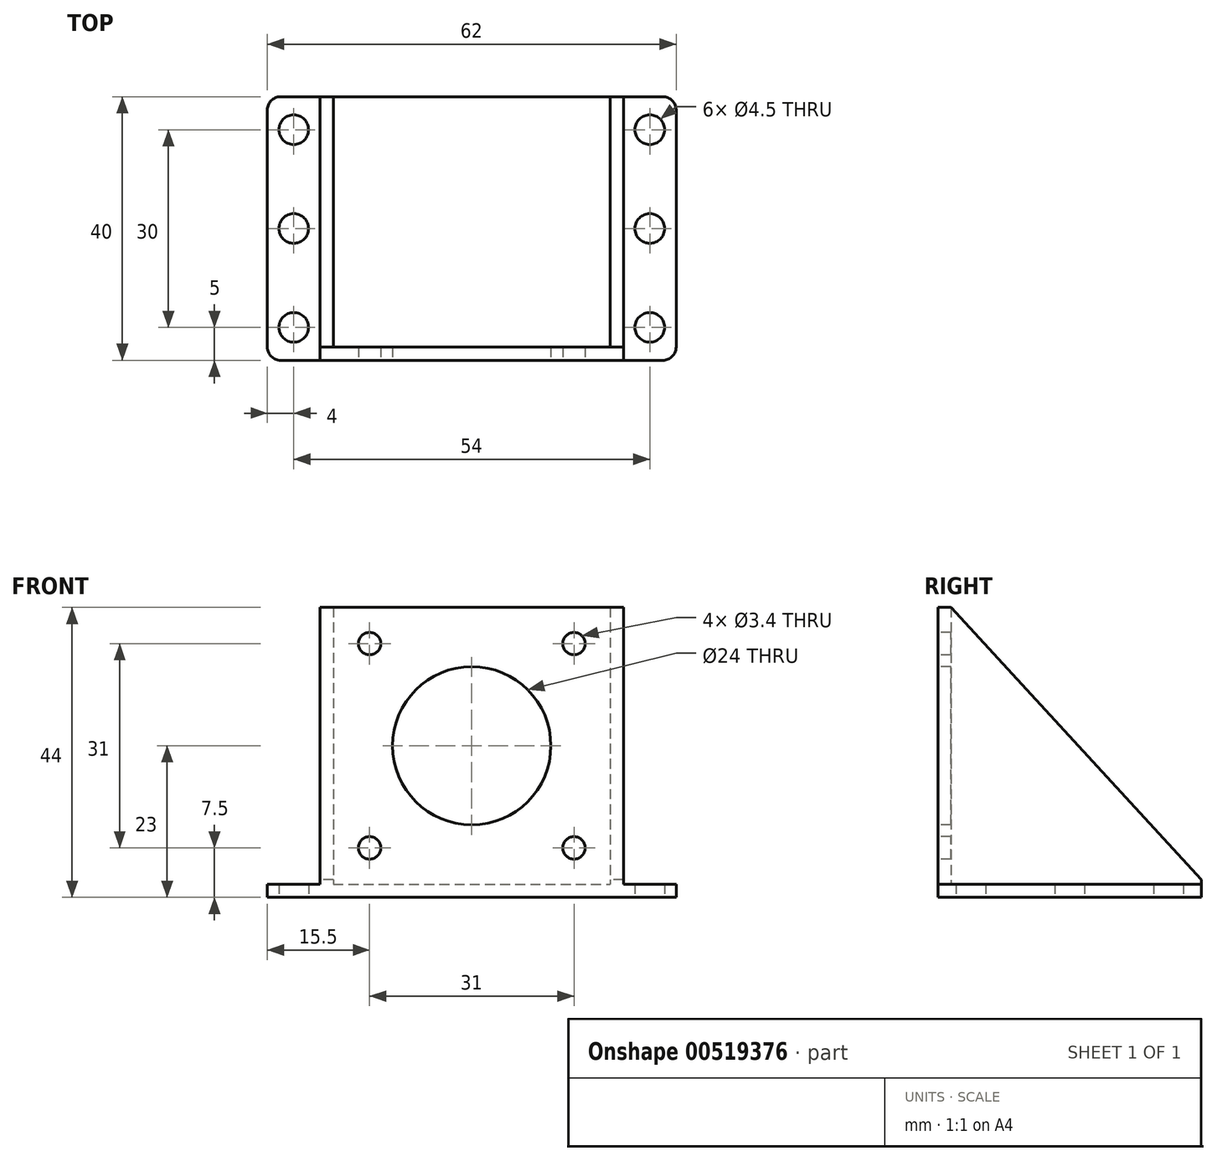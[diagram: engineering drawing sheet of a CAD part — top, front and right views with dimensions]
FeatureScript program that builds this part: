
annotation { "Feature Type Name" : "Feature", "Feature Type Description" : "" }
export const myFeature = defineFeature(function(context is Context, id is Id, definition is map)
    precondition{}
    {
        {
            var Q0;
            Q0=qCreatedBy(makeId("Top.planeOp"),FACE);
            var sketch = newSketch(context, id + "F0", { "sketchPlane" : qUnion([Q0])});
            skLineSegment(sketch, "E0.bottom", {"start": v(2, 0) * mm, "end": v(60, 0) * mm});
            skLineSegment(sketch, "E0.top", {"start": v(2, 40) * mm, "end": v(60, 40) * mm});
            skLineSegment(sketch, "E0.left", {"start": v(0, 2) * mm, "end": v(0, 38) * mm});
            skLineSegment(sketch, "E0.right", {"start": v(62, 2) * mm, "end": v(62, 38) * mm});
            skCircle(sketch, "E1", {"center": v(4, 35) * mm, "radius": 2.25 * mm});
            skCircle(sketch, "E2", {"center": v(4, 20) * mm, "radius": 2.25 * mm});
            skCircle(sketch, "E3", {"center": v(4, 5) * mm, "radius": 2.25 * mm});
            skCircle(sketch, "E4", {"center": v(58, 35) * mm, "radius": 2.25 * mm});
            skCircle(sketch, "E5", {"center": v(58, 20) * mm, "radius": 2.25 * mm});
            skCircle(sketch, "E6", {"center": v(58, 5) * mm, "radius": 2.25 * mm});
            skPoint(sketch, "E7.visualSharp", {"position": v(0, 40) * mm});
            skArc(sketch, "E7.filletArc", {"start": v(2, 40) * mm, "mid": v(0.59, 39.41) * mm, "end": v(0, 38) * mm});
            skPoint(sketch, "E8.visualSharp", {"position": v(0, 0) * mm});
            skArc(sketch, "E8.filletArc", {"start": v(0, 2) * mm, "mid": v(0.59, 0.59) * mm, "end": v(2, 0) * mm});
            skPoint(sketch, "E9.visualSharp", {"position": v(62, 40) * mm});
            skArc(sketch, "E9.filletArc", {"start": v(62, 38) * mm, "mid": v(61.41, 39.41) * mm, "end": v(60, 40) * mm});
            skPoint(sketch, "E10.visualSharp", {"position": v(62, 0) * mm});
            skArc(sketch, "E10.filletArc", {"start": v(60, 0) * mm, "mid": v(61.41, 0.59) * mm, "end": v(62, 2) * mm});
            skSolve(sketch);
        }
        {
            var Q0;
            Q0 = qSketchRegion(id + "F0", true);
            extrude(context, id + "F1", {"entities" : qUnion([Q0]), "depth" : 2 * mm, "offsetDistance" : 25 * mm});
        }
        {
            var Q0;
            Q0=qCreatedBy(makeId("Front.planeOp"),FACE);
            var sketch = newSketch(context, id + "F2", { "sketchPlane" : qUnion([Q0])});
            skLineSegment(sketch, "E11.bottom", {"start": v(8, 0) * mm, "end": v(54, 0) * mm});
            skLineSegment(sketch, "E11.top", {"start": v(8, 44) * mm, "end": v(54, 44) * mm});
            skLineSegment(sketch, "E11.left", {"start": v(8, 0) * mm, "end": v(8, 44) * mm});
            skLineSegment(sketch, "E11.right", {"start": v(54, 0) * mm, "end": v(54, 44) * mm});
            skCircle(sketch, "E12", {"center": v(31, 23) * mm, "radius": 12 * mm});
            skCircle(sketch, "E13", {"center": v(15.5, 38.5) * mm, "radius": 1.7 * mm});
            skCircle(sketch, "E14", {"center": v(15.5, 7.5) * mm, "radius": 1.7 * mm});
            skCircle(sketch, "E15", {"center": v(46.5, 38.5) * mm, "radius": 1.7 * mm});
            skCircle(sketch, "E16", {"center": v(46.5, 7.5) * mm, "radius": 1.7 * mm});
            skSolve(sketch);
        }
        {
            var Q0;
            Q0 = qSketchRegion(id + "F2", true);
            extrude(context, id + "F3", {"entities" : qUnion([Q0]), "operationType" : NewBodyOperationType.ADD, "oppositeDirection" : true, "depth" : 2 * mm, "offsetDistance" : 25 * mm});
        }
        {
            var Q0;
            Q0=makeQuery(id+"F3.opExtrude","SWEPT_FACE",FACE,{"disambiguationData":[OSD([sQuery(id+"F2.wireOp",EDGE,"E11.left")])]});
            var sketch = newSketch(context, id + "F4", { "sketchPlane" : qUnion([Q0])});
            skLineSegment(sketch, "E17", {"start": v(-2, 44) * mm, "end": v(-40, 2.7) * mm});
            skLineSegment(sketch, "E18", {"start": v(-40, 2.7) * mm, "end": v(-40, 0) * mm});
            skLineSegment(sketch, "E19", {"start": v(-40, 0) * mm, "end": v(0, 0) * mm});
            skLineSegment(sketch, "E20", {"start": v(0, 0) * mm, "end": v(0, 44) * mm});
            skLineSegment(sketch, "E21", {"start": v(0, 44) * mm, "end": v(-2, 44) * mm});
            skSolve(sketch);
        }
        {
            var Q0;
            Q0 = qSketchRegion(id + "F4", true);
            extrude(context, id + "F5", {"entities" : qUnion([Q0]), "operationType" : NewBodyOperationType.ADD, "oppositeDirection" : true, "depth" : 2 * mm, "offsetDistance" : 25 * mm});
        }
        {
            var Q0;
            Q0 = qSketchRegion(id + "F4", true);
            extrude(context, id + "F6", {"entities" : qUnion([Q0]), "operationType" : NewBodyOperationType.ADD, "oppositeDirection" : true, "depth" : 46 * mm, "offsetDistance" : 25 * mm, "hasSecondDirection" : true, "secondDirectionOppositeDirection" : true, "secondDirectionDepth" : 44 * mm});
        }
    });
